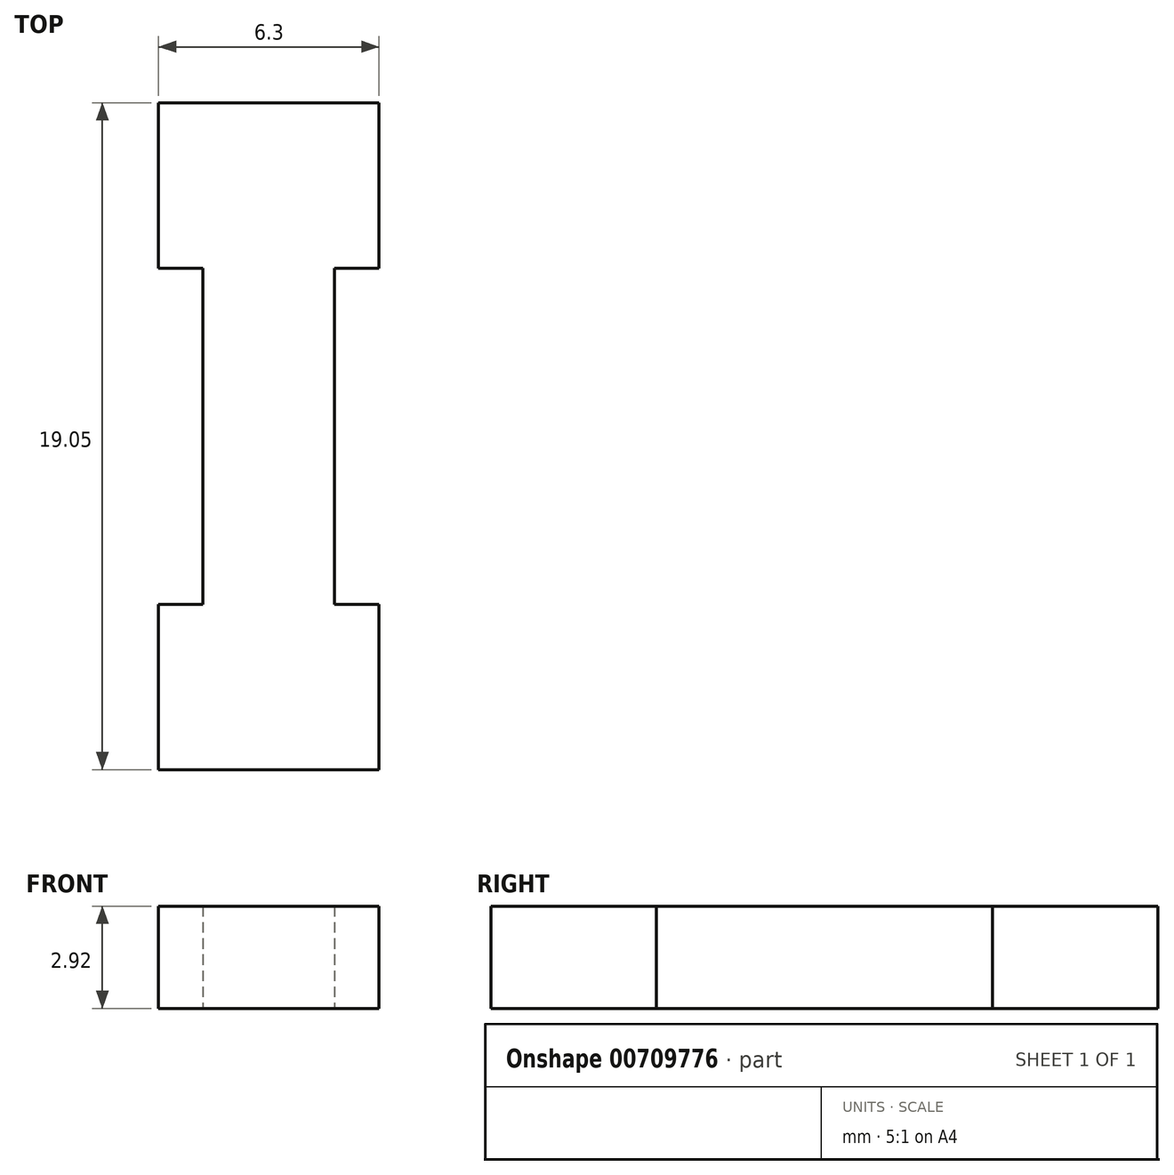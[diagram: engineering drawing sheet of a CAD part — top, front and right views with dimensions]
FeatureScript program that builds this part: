
annotation { "Feature Type Name" : "Feature", "Feature Type Description" : "" }
export const myFeature = defineFeature(function(context is Context, id is Id, definition is map)
    precondition{}
    {
        {
            var Q0;
            Q0=qCreatedBy(makeId("Top.planeOp"),FACE);
            var sketch = newSketch(context, id + "F0", { "sketchPlane" : qUnion([Q0])});
            skLineSegment(sketch, "E0.bottom", {"start": v(3.15, 2.36) * mm, "end": v(-3.15, 2.36) * mm});
            skLineSegment(sketch, "E0.top", {"start": v(3.15, -2.36) * mm, "end": v(-3.15, -2.36) * mm});
            skLineSegment(sketch, "E0.left", {"start": v(3.15, 2.36) * mm, "end": v(3.15, -2.36) * mm});
            skLineSegment(sketch, "E0.right", {"start": v(-3.15, 2.36) * mm, "end": v(-3.15, -2.36) * mm});
            skPoint(sketch, "E0.middle", {"position": v(0, 0) * mm});
            skLineSegment(sketch, "E1", {"start": v(0, 2.36) * mm, "end": v(0, 7.16) * mm});
            skLineSegment(sketch, "E2", {"start": v(0, 7.16) * mm, "end": v(1.88, 7.16) * mm});
            skLineSegment(sketch, "E3", {"start": v(0, 7.16) * mm, "end": v(-1.88, 7.16) * mm});
            skLineSegment(sketch, "E4", {"start": v(-1.88, 7.16) * mm, "end": v(-1.88, 2.36) * mm});
            skLineSegment(sketch, "E5", {"start": v(1.88, 7.16) * mm, "end": v(1.88, 2.36) * mm});
            skLineSegment(sketch, "E6", {"start": v(1.88, 7.16) * mm, "end": v(5.69, 7.16) * mm});
            skLineSegment(sketch, "E7", {"start": v(-1.88, 7.16) * mm, "end": v(-5.69, 7.16) * mm});
            skLineSegment(sketch, "E8", {"start": v(0, 51.61) * mm, "end": v(0, 54.79) * mm});
            skLineSegment(sketch, "E9", {"start": v(0, 54.79) * mm, "end": v(1.9, 54.79) * mm});
            skLineSegment(sketch, "E10", {"start": v(0, 54.79) * mm, "end": v(-1.9, 54.79) * mm});
            skLineSegment(sketch, "E11", {"start": v(-1.9, 54.79) * mm, "end": v(-5.69, 7.16) * mm});
            skLineSegment(sketch, "E12", {"start": v(5.69, 7.16) * mm, "end": v(1.9, 54.79) * mm});
            skSolve(sketch);
        }
        {
            var Q0;
            Q0=makeQuery(id+"F0.imprint","IMPRINT",FACE,{"disambiguationData":[TD([[makeQuery(id+"F0.imprint","IMPRINT",EDGE,{"derivedFrom":sQuery(id+"F0.wireOp",EDGE,"E0.top")}),-1.0]])]});
            var Q1;
            {var subQ0=sQuery(id+"F0.wireOp",EDGE,"E1");Q1=makeQuery(id+"F0.imprint","IMPRINT",FACE,{"disambiguationData":[TD([[makeQuery(id+"F0.imprint","IMPRINT",EDGE,{"derivedFrom":subQ0}),-1.0]])]});}
            var Q2;
            {var subQ0=sQuery(id+"F0.wireOp",EDGE,"E1");Q2=makeQuery(id+"F0.imprint","IMPRINT",FACE,{"disambiguationData":[TD([[makeQuery(id+"F0.imprint","IMPRINT",EDGE,{"derivedFrom":subQ0}),1.0]])]});}
            extrude(context, id + "F1", {"entities" : qUnion([Q0, Q1, Q2]), "depth" : 2.92 * mm, "offsetDistance" : 25.4 * mm});
        }
        {
            var Q0;
            Q0=makeQuery(id+"F1.opExtrude","SWEPT_BODY",BODY,{"disambiguationData":[OSD([sQuery(id+"F0.wireOp",EDGE,"E0.bottom"),sQuery(id+"F0.wireOp",EDGE,"E0.top"),sQuery(id+"F0.wireOp",EDGE,"E0.left"),sQuery(id+"F0.wireOp",EDGE,"E0.right"),sQuery(id+"F0.wireOp",EDGE,"E2"),sQuery(id+"F0.wireOp",EDGE,"E3"),sQuery(id+"F0.wireOp",EDGE,"E4"),sQuery(id+"F0.wireOp",EDGE,"E5")])]});
            var Q1;
            Q1=makeQuery(id+"F1.opExtrude","SWEPT_FACE",FACE,{"disambiguationData":[OSD([sQuery(id+"F0.wireOp",EDGE,"E2"),sQuery(id+"F0.wireOp",EDGE,"E3")])]});
            mirror(context, id + "F2", {"operationType" : NewBodyOperationType.ADD, "entities" : qUnion([Q0]), "mirrorPlane" : qUnion([Q1])});
        }
    });
